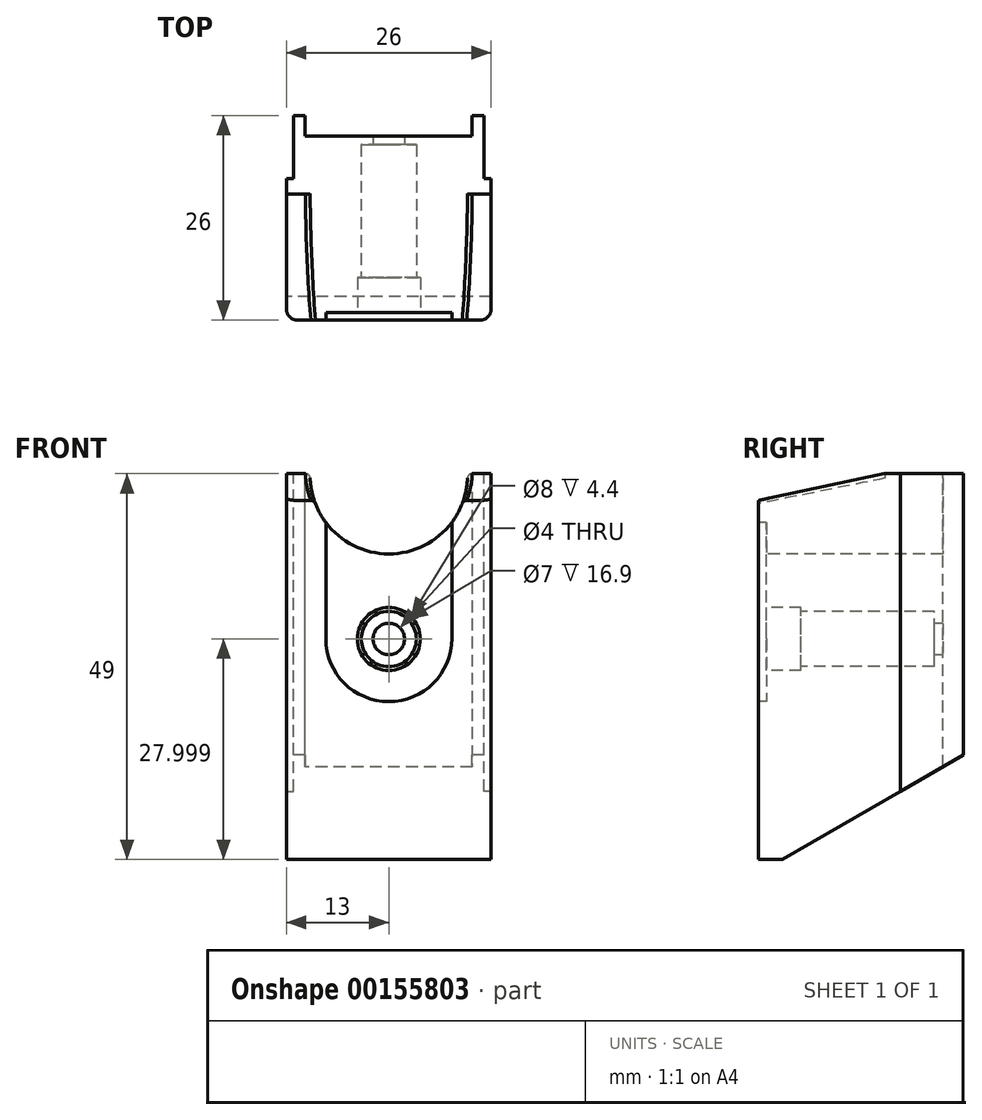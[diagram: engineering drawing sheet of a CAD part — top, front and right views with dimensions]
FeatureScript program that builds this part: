
annotation { "Feature Type Name" : "Feature", "Feature Type Description" : "" }
export const myFeature = defineFeature(function(context is Context, id is Id, definition is map)
    precondition{}
    {
        {
            var Q0;
            Q0=qCreatedBy(makeId("Right.planeOp"),FACE);
            var sketch = newSketch(context, id + "F0", { "sketchPlane" : qUnion([Q0])});
            skLineSegment(sketch, "E0", {"start": v(-26, 25.48) * mm, "end": v(-26, -20.13) * mm});
            skLineSegment(sketch, "E1", {"start": v(-26, -20.13) * mm, "end": v(-23, -20.13) * mm});
            skLineSegment(sketch, "E2", {"start": v(0, 28.87) * mm, "end": v(0, -6.85) * mm});
            skLineSegment(sketch, "E3", {"start": v(0, 28.87) * mm, "end": v(-10, 28.87) * mm});
            skLineSegment(sketch, "E4", {"start": v(-10, 28.87) * mm, "end": v(-26, 25.48) * mm});
            skLineSegment(sketch, "E5", {"start": v(-23, -20.13) * mm, "end": v(0, -6.85) * mm});
            skLineSegment(sketch, "E6", {"start": v(11.71, 28.87) * mm, "end": v(-47.25, 28.87) * mm, "construction": true});
            skPoint(sketch, "E6.endSnap0", {"position": v(-5, 28.87) * mm});
            skLineSegment(sketch, "E7", {"start": v(-47.25, -20.13) * mm, "end": v(12.12, -20.13) * mm, "construction": true});
            skSolve(sketch);
        }
        {
            var Q0;
            Q0 = qSketchRegion(id + "F0", true);
            extrude(context, id + "F1", {"entities" : qUnion([Q0]), "depth" : 26 * mm});
        }
        {
            var Q0;
            Q0=makeQuery(id+"F1.opExtrude","SWEPT_FACE",FACE,{"disambiguationData":[OSD([sQuery(id+"F0.wireOp",EDGE,"E0")])]});
            var sketch = newSketch(context, id + "F2", { "sketchPlane" : qUnion([Q0])});
            skLineSegment(sketch, "E8", {"start": v(13, 41.2) * mm, "end": v(13, -40.79) * mm, "construction": true});
            skPoint(sketch, "E8.startSnap0", {"position": v(13, 25.48) * mm});
            skPoint(sketch, "E8.endSnap0", {"position": v(13, -20.13) * mm});
            skLineSegment(sketch, "E9", {"start": v(-15.14, 7.87) * mm, "end": v(44.62, 7.87) * mm, "construction": true});
            skCircle(sketch, "E10", {"center": v(13, 28.67) * mm, "radius": 10 * mm});
            skCircle(sketch, "E11", {"center": v(13, 7.87) * mm, "radius": 2 * mm});
            skSolve(sketch);
        }
        {
            var Q0;
            Q0 = qSketchRegion(id + "F2", true);
            extrude(context, id + "F3", {"entities" : qUnion([Q0]), "operationType" : NewBodyOperationType.REMOVE, "oppositeDirection" : true, "depth" : 26 * mm});
        }
        {
            var Q0;
            Q0=makeQuery(id+"F1.opExtrude","SWEPT_FACE",FACE,{"disambiguationData":[OSD([sQuery(id+"F0.wireOp",EDGE,"E0")])]});
            var sketch = newSketch(context, id + "F4", { "sketchPlane" : qUnion([Q0])});
            skLineSegment(sketch, "E12", {"start": v(13, 7.87) * mm, "end": v(30.7, 7.87) * mm, "construction": true});
            skLineSegment(sketch, "E13", {"start": v(13, 7.87) * mm, "end": v(13, 31.85) * mm, "construction": true});
            skPoint(sketch, "E13.endSnap0", {"position": v(13, 18.67) * mm});
            skCircle(sketch, "E14", {"center": v(13, 7.87) * mm, "radius": 3.5 * mm});
            skCircle(sketch, "E15", {"center": v(13, 7.87) * mm, "radius": 2 * mm});
            skSolve(sketch);
        }
        {
            var Q0;
            Q0 = qSketchRegion(id + "F4", true);
            extrude(context, id + "F5", {"entities" : qUnion([Q0]), "operationType" : NewBodyOperationType.REMOVE, "oppositeDirection" : true, "depth" : 22.3 * mm});
        }
        {
            var Q0;
            Q0=makeQuery(id+"F1.opExtrude","SWEPT_FACE",FACE,{"disambiguationData":[OSD([sQuery(id+"F0.wireOp",EDGE,"E0")])]});
            var sketch = newSketch(context, id + "F6", { "sketchPlane" : qUnion([Q0])});
            skCircle(sketch, "E16", {"center": v(13, 7.87) * mm, "radius": 4 * mm});
            skCircle(sketch, "E17", {"center": v(13, 7.87) * mm, "radius": 3.5 * mm});
            skSolve(sketch);
        }
        {
            var Q0;
            Q0 = qSketchRegion(id + "F6", true);
            extrude(context, id + "F7", {"entities" : qUnion([Q0]), "operationType" : NewBodyOperationType.REMOVE, "oppositeDirection" : true, "depth" : 5.4 * mm});
        }
        {
            var Q0;
            Q0=makeQuery(id+"F3.boolean.opBoolean","INTERSECT",EDGE,{"disambiguationData":[OD(0.0)],"derivedFrom":[makeQuery(id+"F1.opExtrude","SWEPT_FACE",FACE,{"disambiguationData":[OSD([sQuery(id+"F0.wireOp",EDGE,"E4")])]}),makeQuery(id+"F3.opExtrude","SWEPT_FACE",FACE,{"disambiguationData":[OSD([sQuery(id+"F2.wireOp",EDGE,"E10")])]})]});
            var Q1;
            Q1=makeQuery(id+"F3.boolean.opBoolean","INTERSECT",EDGE,{"disambiguationData":[OD(0.0)],"derivedFrom":[makeQuery(id+"F1.opExtrude","SWEPT_FACE",FACE,{"disambiguationData":[OSD([sQuery(id+"F0.wireOp",EDGE,"E3")])]}),makeQuery(id+"F3.opExtrude","SWEPT_FACE",FACE,{"disambiguationData":[OSD([sQuery(id+"F2.wireOp",EDGE,"E10")])]})]});
            var Q2;
            Q2=makeQuery(id+"F3.boolean.opBoolean","INTERSECT",EDGE,{"disambiguationData":[OD(1.0)],"derivedFrom":[makeQuery(id+"F1.opExtrude","SWEPT_FACE",FACE,{"disambiguationData":[OSD([sQuery(id+"F0.wireOp",EDGE,"E3")])]}),makeQuery(id+"F3.opExtrude","SWEPT_FACE",FACE,{"disambiguationData":[OSD([sQuery(id+"F2.wireOp",EDGE,"E10")])]})]});
            var Q3;
            Q3=makeQuery(id+"F3.boolean.opBoolean","INTERSECT",EDGE,{"disambiguationData":[OD(1.0)],"derivedFrom":[makeQuery(id+"F1.opExtrude","SWEPT_FACE",FACE,{"disambiguationData":[OSD([sQuery(id+"F0.wireOp",EDGE,"E4")])]}),makeQuery(id+"F3.opExtrude","SWEPT_FACE",FACE,{"disambiguationData":[OSD([sQuery(id+"F2.wireOp",EDGE,"E10")])]})]});
            fillet(context, id + "F8", {"entities" : qUnion([Q0, Q1, Q2, Q3]), "radius" : .6 * mm, "tangentPropagation" : true, "allowEdgeOverflow" : false});
        }
        {
            var Q0;
            {var subQ0=sQuery(id+"F0.wireOp",EDGE,"E4");var subQ1=sQuery(id+"F0.wireOp",EDGE,"E3");var subQ2=sQuery(id+"F0.wireOp",EDGE,"E2");Q0=makeQuery(id+"F3.boolean.opBoolean","SPLIT",FACE,{"disambiguationData":[TD([makeQuery(id+"F1.opExtrude","CAP_FACE",FACE,{"disambiguationData":[OSD([sQuery(id+"F0.wireOp",EDGE,"E0"),sQuery(id+"F0.wireOp",EDGE,"E1"),subQ2,subQ1,subQ0,sQuery(id+"F0.wireOp",EDGE,"E5")])],"isStart":false})])],"derivedFrom":makeQuery(id+"F1.opExtrude","SWEPT_FACE",FACE,{"disambiguationData":[OSD([subQ1])]})});}
            var sketch = newSketch(context, id + "F9", { "sketchPlane" : qUnion([Q0])});
            skLineSegment(sketch, "E18", {"start": v(13, -17.3) * mm, "end": v(13, 6.03) * mm, "construction": true});
            skLineSegment(sketch, "E19", {"start": v(26, -8) * mm, "end": v(25.07, -8) * mm});
            skLineSegment(sketch, "E20", {"start": v(25.07, -8) * mm, "end": v(25.07, 0) * mm});
            skLineSegment(sketch, "E21", {"start": v(25.07, 0) * mm, "end": v(26, 0) * mm});
            skLineSegment(sketch, "E22", {"start": v(26, 0) * mm, "end": v(26, -8) * mm});
            skLineSegment(sketch, "E23.MirrorCS", {"start": v(0.93, -8) * mm, "end": v(0.93, 0) * mm});
            skLineSegment(sketch, "E24.MirrorCS", {"start": v(0, 0) * mm, "end": v(0, -8) * mm});
            skLineSegment(sketch, "E25.MirrorCS", {"start": v(0, -8) * mm, "end": v(0.93, -8) * mm});
            skLineSegment(sketch, "E26.MirrorCS", {"start": v(0.93, 0) * mm, "end": v(0, 0) * mm});
            skSolve(sketch);
        }
        {
            var Q0;
            Q0 = qSketchRegion(id + "F9", true);
            extrude(context, id + "F10", {"entities" : qUnion([Q0]), "operationType" : NewBodyOperationType.REMOVE, "oppositeDirection" : true, "depth" : 61.5 * mm});
        }
        {
            var Q0;
            Q0=makeQuery(id+"F1.opExtrude","CAP_EDGE",EDGE,{"disambiguationData":[OSD([sQuery(id+"F0.wireOp",EDGE,"E0")])],"isStart":true});
            var Q1;
            Q1=makeQuery(id+"F1.opExtrude","CAP_EDGE",EDGE,{"disambiguationData":[OSD([sQuery(id+"F0.wireOp",EDGE,"E0")])],"isStart":false});
            var Q2;
            Q2=makeQuery(id+"F10.boolean.opBoolean","COPY",EDGE,{"derivedFrom":makeQuery(id+"F10.opExtrude","SWEPT_EDGE",EDGE,{"disambiguationData":[OSD([sQuery(id+"F9.wireOp",EDGE,"E26.MirrorCS"),sQuery(id+"F9.wireOp",EDGE,"E23.MirrorCS")])]})});
            var Q3;
            Q3=makeQuery(id+"F10.boolean.opBoolean","COPY",EDGE,{"derivedFrom":makeQuery(id+"F10.opExtrude","SWEPT_EDGE",EDGE,{"disambiguationData":[OSD([sQuery(id+"F0.wireOp",EDGE,"E2"),sQuery(id+"F0.wireOp",EDGE,"E3"),sQuery(id+"F9.wireOp",EDGE,"E20"),sQuery(id+"F9.wireOp",EDGE,"E21")])]})});
            fillet(context, id + "F11", {"entities" : qUnion([Q0, Q1, Q2, Q3]), "radius" : 1.4 * mm, "tangentPropagation" : true, "allowEdgeOverflow" : false});
        }
        {
            var Q0;
            Q0=makeQuery(id+"F1.opExtrude","SWEPT_FACE",FACE,{"disambiguationData":[OSD([sQuery(id+"F0.wireOp",EDGE,"E2")])]});
            var sketch = newSketch(context, id + "F12", { "sketchPlane" : qUnion([Q0])});
            skLineSegment(sketch, "E27", {"start": v(-23.6, 31.71) * mm, "end": v(-23.6, -10.62) * mm});
            skLineSegment(sketch, "E28", {"start": v(-23.6, -10.62) * mm, "end": v(-2.33, -10.62) * mm});
            skLineSegment(sketch, "E29", {"start": v(-2.33, -10.62) * mm, "end": v(-2.33, 31.71) * mm});
            skLineSegment(sketch, "E30", {"start": v(-2.33, 31.71) * mm, "end": v(-23.6, 31.71) * mm});
            skSolve(sketch);
        }
        {
            var Q0;
            Q0 = qSketchRegion(id + "F12", true);
            extrude(context, id + "F13", {"entities" : qUnion([Q0]), "operationType" : NewBodyOperationType.REMOVE, "oppositeDirection" : true, "depth" : 2.6 * mm});
        }
        {
            var Q0;
            Q0=makeQuery(id+"F1.opExtrude","SWEPT_FACE",FACE,{"disambiguationData":[OSD([sQuery(id+"F0.wireOp",EDGE,"E0")])]});
            var sketch = newSketch(context, id + "F14", { "sketchPlane" : qUnion([Q0])});
            skPoint(sketch, "E31.startSnap0", {"position": v(13, 18.67) * mm});
            skPoint(sketch, "E31.endSnap0", {"position": v(13, -20.13) * mm});
            skLineSegment(sketch, "E32", {"start": v(13, 21.82) * mm, "end": v(13, -22.95) * mm, "construction": true});
            skLineSegment(sketch, "E33", {"start": v(-2.79, 7.91) * mm, "end": v(28.47, 7.91) * mm, "construction": true});
            skCircle(sketch, "E34", {"center": v(13, 7.91) * mm, "radius": 8 * mm});
            skLineSegment(sketch, "E35", {"start": v(5, 7.91) * mm, "end": v(5, 25.78) * mm});
            skLineSegment(sketch, "E36", {"start": v(21, 7.91) * mm, "end": v(21, 25.78) * mm});
            skLineSegment(sketch, "E37", {"start": v(5, 25.78) * mm, "end": v(21, 25.78) * mm});
            skSolve(sketch);
        }
        {
            var Q0;
            Q0 = qSketchRegion(id + "F14", true);
            extrude(context, id + "F15", {"entities" : qUnion([Q0]), "operationType" : NewBodyOperationType.REMOVE, "oppositeDirection" : true, "depth" : 1 * mm});
        }
    });
